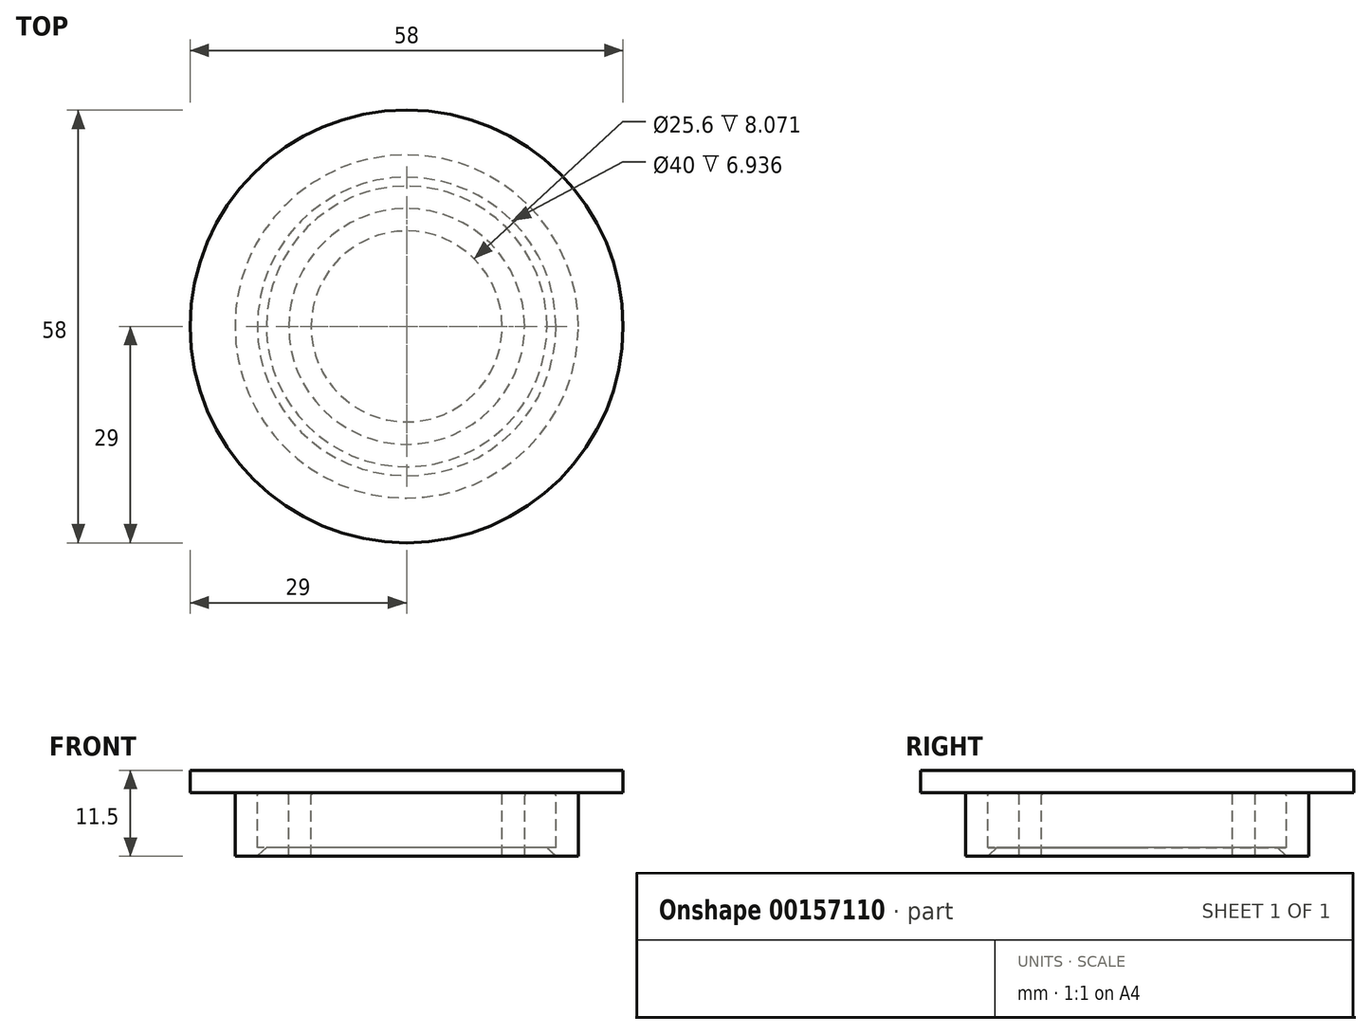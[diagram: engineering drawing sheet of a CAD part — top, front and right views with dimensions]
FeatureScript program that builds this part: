
annotation { "Feature Type Name" : "Feature", "Feature Type Description" : "" }
export const myFeature = defineFeature(function(context is Context, id is Id, definition is map)
    precondition{}
    {
        {
            var Q0;
            Q0=qCreatedBy(makeId("Front.planeOp"),FACE);
            var sketch = newSketch(context, id + "F0", { "sketchPlane" : qUnion([Q0])});
            skLineSegment(sketch, "E0", {"start": v(-15.8, 0) * mm, "end": v(-15.8, 8.07) * mm});
            skLineSegment(sketch, "E1", {"start": v(-16.23, 8.5) * mm, "end": v(-19.57, 8.5) * mm});
            skLineSegment(sketch, "E2", {"start": v(-20, 8.07) * mm, "end": v(-20, 1.13) * mm});
            skLineSegment(sketch, "E3", {"start": v(-20, 0) * mm, "end": v(-23, 0) * mm});
            skLineSegment(sketch, "E4", {"start": v(-23, 0) * mm, "end": v(-23, 8.5) * mm});
            skLineSegment(sketch, "E5", {"start": v(-23, 11.5) * mm, "end": v(0, 11.5) * mm});
            skLineSegment(sketch, "E6", {"start": v(0, 11.5) * mm, "end": v(0, 8.5) * mm});
            skLineSegment(sketch, "E7", {"start": v(-20, 1.13) * mm, "end": v(-18.8, 1.13) * mm});
            skLineSegment(sketch, "E8", {"start": v(-18.8, 1.13) * mm, "end": v(-20, 0) * mm});
            skLineSegment(sketch, "E9", {"start": v(-15.8, 0) * mm, "end": v(-12.8, 0) * mm});
            skLineSegment(sketch, "E10", {"start": v(-12.8, 0) * mm, "end": v(-12.8, 8.07) * mm});
            skLineSegment(sketch, "E11", {"start": v(-12.37, 8.5) * mm, "end": v(0, 8.5) * mm});
            skPoint(sketch, "E12.visualSharp", {"position": v(-20, 8.5) * mm});
            skArc(sketch, "E12.filletArc", {"start": v(-19.57, 8.5) * mm, "mid": v(-19.87, 8.37) * mm, "end": v(-20, 8.07) * mm});
            skPoint(sketch, "E13.visualSharp", {"position": v(-15.8, 8.5) * mm});
            skArc(sketch, "E13.filletArc", {"start": v(-15.8, 8.07) * mm, "mid": v(-15.93, 8.37) * mm, "end": v(-16.23, 8.5) * mm});
            skPoint(sketch, "E14.visualSharp", {"position": v(-12.8, 8.5) * mm});
            skArc(sketch, "E14.filletArc", {"start": v(-12.37, 8.5) * mm, "mid": v(-12.67, 8.37) * mm, "end": v(-12.8, 8.07) * mm});
            skLineSegment(sketch, "E15", {"start": v(-23, 11.5) * mm, "end": v(-29, 11.5) * mm});
            skLineSegment(sketch, "E16", {"start": v(-29, 11.5) * mm, "end": v(-29, 8.5) * mm});
            skLineSegment(sketch, "E17", {"start": v(-29, 8.5) * mm, "end": v(-23, 8.5) * mm});
            skSolve(sketch);
        }
        {
            var Q0;
            Q0=makeQuery(id+"F0.imprint","IMPRINT",FACE,{"disambiguationData":[TD([[makeQuery(id+"F0.imprint","IMPRINT",EDGE,{"derivedFrom":sQuery(id+"F0.wireOp",EDGE,"E0")}),-1.0]])]});
            var Q1;
            Q1=sQuery(id+"F0.wireOp",EDGE,"E6");
            revolve(context, id + "F1", {"entities" : qUnion([Q0]), "axis" : qUnion([Q1]), "revolveType" : RevolveType.FULL});
        }
    });
